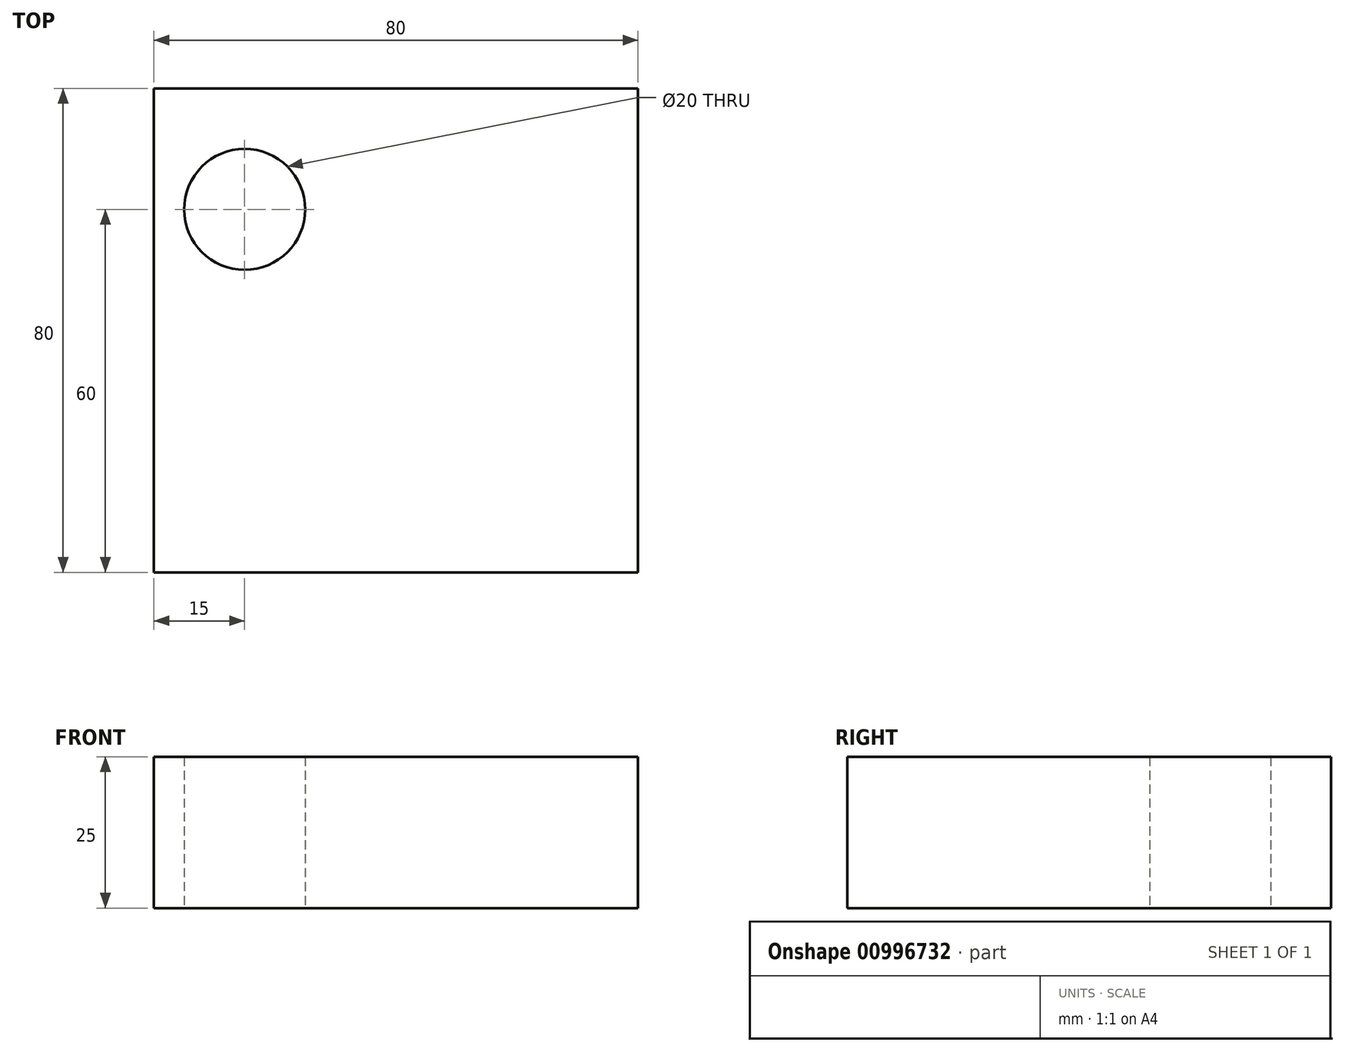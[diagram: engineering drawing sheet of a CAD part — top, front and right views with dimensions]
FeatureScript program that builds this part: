
annotation { "Feature Type Name" : "Feature", "Feature Type Description" : "" }
export const myFeature = defineFeature(function(context is Context, id is Id, definition is map)
    precondition{}
    {
        {
            var Q0;
            Q0=qCreatedBy(makeId("Top.planeOp"),FACE);
            var sketch = newSketch(context, id + "F0", { "sketchPlane" : qUnion([Q0])});
            skLineSegment(sketch, "E0.bottom", {"start": v(40, -40) * mm, "end": v(-40, -40) * mm});
            skLineSegment(sketch, "E0.top", {"start": v(40, 40) * mm, "end": v(-40, 40) * mm});
            skLineSegment(sketch, "E0.left", {"start": v(40, -40) * mm, "end": v(40, 40) * mm});
            skLineSegment(sketch, "E0.right", {"start": v(-40, -40) * mm, "end": v(-40, 40) * mm});
            skPoint(sketch, "E0.middle", {"position": v(0, 0) * mm});
            skCircle(sketch, "E1", {"center": v(-25, 20) * mm, "radius": 10 * mm});
            skSolve(sketch);
        }
        {
            var Q0;
            Q0=makeQuery(id+"F0.imprint","IMPRINT",FACE,{"disambiguationData":[TD([[makeQuery(id+"F0.imprint","IMPRINT",EDGE,{"derivedFrom":sQuery(id+"F0.wireOp",EDGE,"E0.bottom")}),-1.0]])]});
            extrude(context, id + "F1", {"entities" : qUnion([Q0]), "depth" : 25 * mm, "offsetDistance" : 25 * mm});
        }
    });
